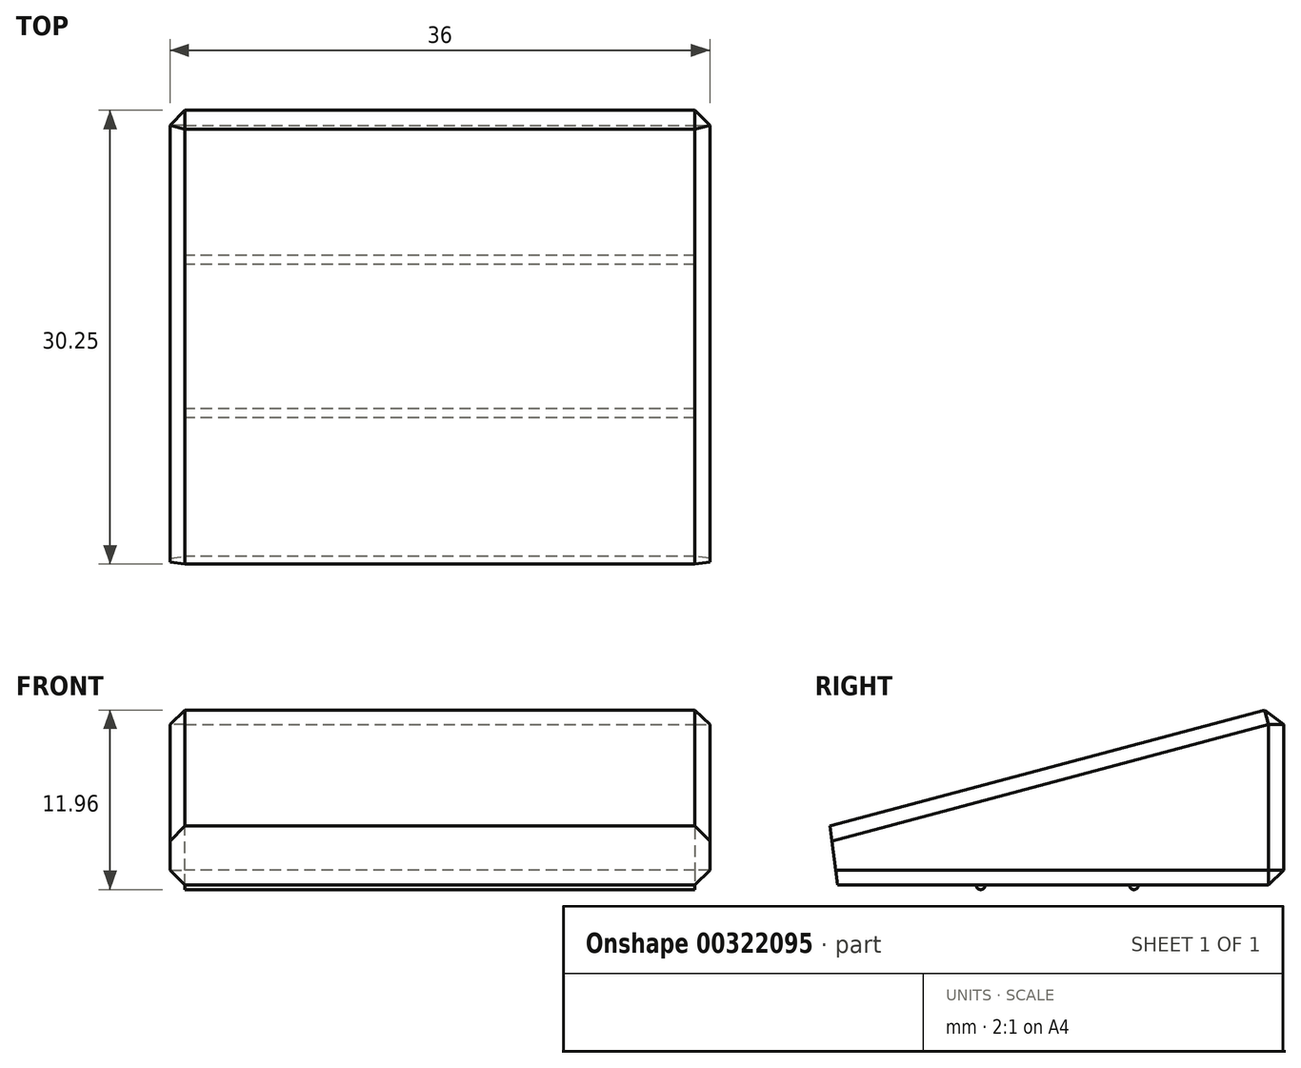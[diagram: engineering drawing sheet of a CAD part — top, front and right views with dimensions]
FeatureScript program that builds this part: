
annotation { "Feature Type Name" : "Feature", "Feature Type Description" : "" }
export const myFeature = defineFeature(function(context is Context, id is Id, definition is map)
    precondition{}
    {
        {
            var Q0;
            Q0=qCreatedBy(makeId("Front.planeOp"),FACE);
            var sketch = newSketch(context, id + "F0", { "sketchPlane" : qUnion([Q0])});
            skLineSegment(sketch, "E0.bottom", {"start": v(0, 0) * mm, "end": v(36, 0) * mm});
            skLineSegment(sketch, "E0.top", {"start": v(0, -12) * mm, "end": v(36, -12) * mm});
            skLineSegment(sketch, "E0.left", {"start": v(0, 0) * mm, "end": v(0, -12) * mm});
            skLineSegment(sketch, "E0.right", {"start": v(36, 0) * mm, "end": v(36, -12) * mm});
            skSolve(sketch);
        }
        {
            var Q0;
            Q0=qCreatedBy(makeId("Right.planeOp"),FACE);
            var sketch = newSketch(context, id + "F1", { "sketchPlane" : qUnion([Q0])});
            skPoint(sketch, "E1.0", {"position": v(0, -12) * mm});
            skLineSegment(sketch, "E2", {"start": v(0, -12) * mm, "end": v(-45, -12) * mm});
            skLineSegment(sketch, "E3", {"start": v(-45, -12) * mm, "end": v(0, 0) * mm});
            skLineSegment(sketch, "E4", {"start": v(0, 0) * mm, "end": v(0, -12) * mm});
            skSolve(sketch);
        }
        {
            var Q0;
            Q0=makeQuery(id+"F1.imprint","IMPRINT",FACE,{"disambiguationData":[TD([[makeQuery(id+"F1.imprint","IMPRINT",EDGE,{"derivedFrom":sQuery(id+"F1.wireOp",EDGE,"E2")}),-1.0]])]});
            var Q1;
            Q1=sQuery(id+"F0.wireOp",VERTEX,"E0.right.start");
            extrude(context, id + "F2", {"entities" : qUnion([Q0]), "endBound" : BoundingType.UP_TO_VERTEX, "endBoundEntityVertex" : qUnion([Q1]), "depth" : 25 * mm});
        }
        {
            var Q0;
            Q0=makeQuery(id+"F2.opExtrude","CAP_EDGE",EDGE,{"disambiguationData":[OSD([sQuery(id+"F1.wireOp",EDGE,"E3")])],"isStart":false});
            var Q1;
            Q1=makeQuery(id+"F2.opExtrude","CAP_EDGE",EDGE,{"disambiguationData":[OSD([sQuery(id+"F1.wireOp",EDGE,"E3")])],"isStart":true});
            var Q2;
            Q2=makeQuery(id+"F2.opExtrude","CAP_EDGE",EDGE,{"disambiguationData":[OSD([sQuery(id+"F1.wireOp",EDGE,"E2")])],"isStart":false});
            var Q3;
            Q3=makeQuery(id+"F2.opExtrude","CAP_EDGE",EDGE,{"disambiguationData":[OSD([sQuery(id+"F1.wireOp",EDGE,"E4")])],"isStart":false});
            var Q4;
            Q4=makeQuery(id+"F2.opExtrude","CAP_EDGE",EDGE,{"disambiguationData":[OSD([sQuery(id+"F1.wireOp",EDGE,"E2")])],"isStart":true});
            var Q5;
            Q5=makeQuery(id+"F2.opExtrude","CAP_EDGE",EDGE,{"disambiguationData":[OSD([sQuery(id+"F1.wireOp",EDGE,"E4")])],"isStart":true});
            var Q6;
            Q6=makeQuery(id+"F2.opExtrude","SWEPT_EDGE",EDGE,{"disambiguationData":[OSD([sQuery(id+"F1.wireOp",EDGE,"E3"),sQuery(id+"F1.wireOp",EDGE,"E4")])]});
            var Q7;
            Q7=makeQuery(id+"F2.opExtrude","SWEPT_EDGE",EDGE,{"disambiguationData":[OSD([sQuery(id+"F1.wireOp",EDGE,"E2"),sQuery(id+"F1.wireOp",EDGE,"E4")])]});
            chamfer(context, id + "F3", {"entities" : qUnion([Q0, Q1, Q2, Q3, Q4, Q5, Q6, Q7]), "width" : 1 * mm, "tangentPropagation" : true});
        }
        {
            var Q0;
            Q0=makeQuery(id+"F2.opExtrude","SWEPT_EDGE",EDGE,{"disambiguationData":[OSD([sQuery(id+"F1.wireOp",EDGE,"E2"),sQuery(id+"F1.wireOp",EDGE,"E3")])]});
            chamfer(context, id + "F4", {"entities" : qUnion([Q0]), "width" : 2 * mm, "tangentPropagation" : true});
        }
        {
            var Q0;
            Q0=makeQuery(id+"F2.opExtrude","SWEPT_FACE",FACE,{"disambiguationData":[OSD([sQuery(id+"F1.wireOp",EDGE,"E2")])]});
            var sketch = newSketch(context, id + "F5", { "sketchPlane" : qUnion([Q0])});
            skLineSegment(sketch, "E5.bottom", {"start": v(35, 19.9) * mm, "end": v(1, 19.9) * mm});
            skLineSegment(sketch, "E5.top", {"start": v(35, 20.2) * mm, "end": v(1, 20.2) * mm});
            skLineSegment(sketch, "E5.left", {"start": v(35, 19.9) * mm, "end": v(35, 20.2) * mm});
            skLineSegment(sketch, "E5.right", {"start": v(1, 19.9) * mm, "end": v(1, 20.2) * mm});
            skLineSegment(sketch, "E6.bottom", {"start": v(35, 9.98) * mm, "end": v(1, 9.98) * mm});
            skLineSegment(sketch, "E6.top", {"start": v(35, 10.28) * mm, "end": v(1, 10.28) * mm});
            skLineSegment(sketch, "E6.left", {"start": v(35, 9.98) * mm, "end": v(35, 10.28) * mm});
            skLineSegment(sketch, "E6.right", {"start": v(1, 9.98) * mm, "end": v(1, 10.28) * mm});
            skSolve(sketch);
        }
        {
            var Q0;
            Q0=makeQuery(id+"F5.imprint","IMPRINT",FACE,{"disambiguationData":[TD([[makeQuery(id+"F5.imprint","IMPRINT",EDGE,{"derivedFrom":sQuery(id+"F5.wireOp",EDGE,"E5.bottom")}),-1.0]])]});
            var Q1;
            Q1=sQuery(id+"F5.wireOp",EDGE,"E5.top");
            revolve(context, id + "F6", {"operationType" : NewBodyOperationType.ADD, "entities" : qUnion([Q0]), "axis" : qUnion([Q1]), "revolveType" : RevolveType.ONE_DIRECTION, "angle" : 180 * degree});
        }
        {
            var Q0;
            Q0=makeQuery(id+"F5.imprint","IMPRINT",FACE,{"disambiguationData":[TD([[makeQuery(id+"F5.imprint","IMPRINT",EDGE,{"derivedFrom":sQuery(id+"F5.wireOp",EDGE,"E6.bottom")}),-1.0]])]});
            var Q1;
            Q1=sQuery(id+"F5.wireOp",EDGE,"E6.bottom");
            revolve(context, id + "F7", {"operationType" : NewBodyOperationType.ADD, "entities" : qUnion([Q0]), "axis" : qUnion([Q1]), "revolveType" : RevolveType.ONE_DIRECTION, "oppositeDirection" : true, "angle" : 180 * degree});
        }
    });
